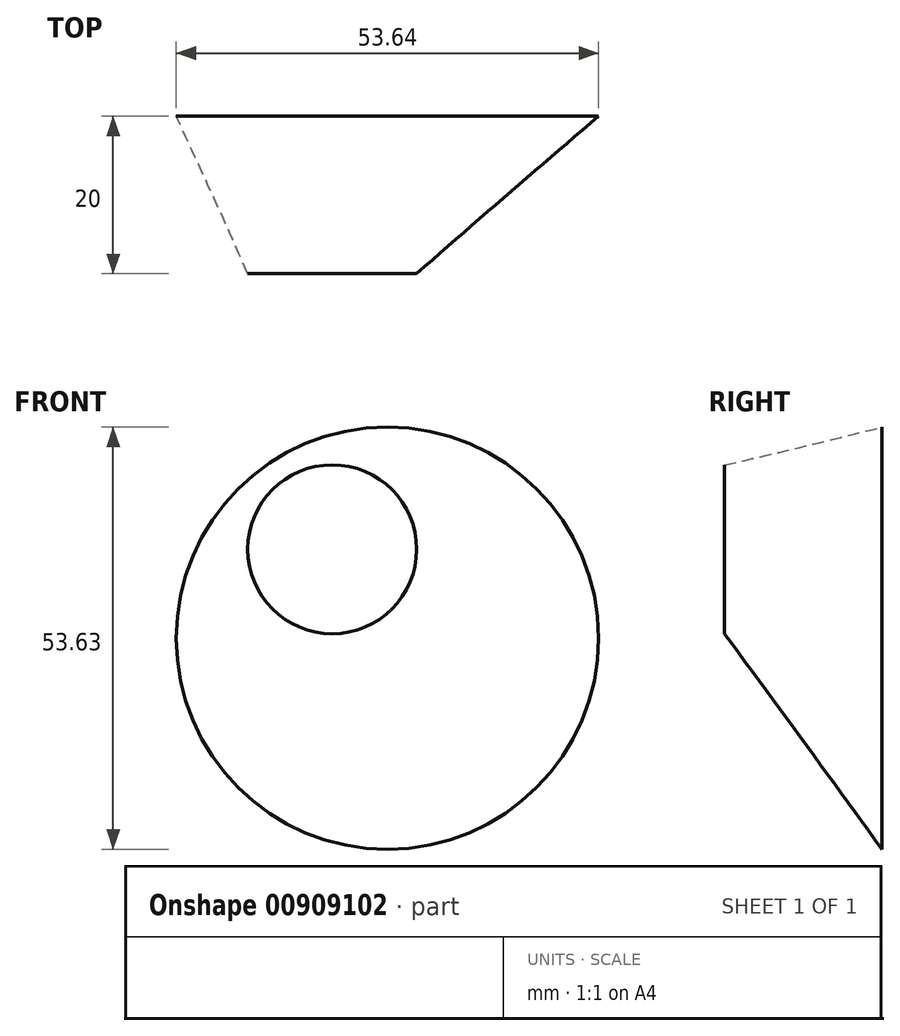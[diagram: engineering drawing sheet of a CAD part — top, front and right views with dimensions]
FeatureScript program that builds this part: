
annotation { "Feature Type Name" : "Feature", "Feature Type Description" : "" }
export const myFeature = defineFeature(function(context is Context, id is Id, definition is map)
    precondition{}
    {
        {
            var Q0;
            Q0=qCreatedBy(makeId("Front.planeOp"),FACE);
            var sketch = newSketch(context, id + "F0", { "sketchPlane" : qUnion([Q0])});
            skCircle(sketch, "E0", {"center": v(58.91, 25.92) * mm, "radius": 26.82 * mm});
            skSolve(sketch);
        }
        {
            var Q0;
            Q0=qCreatedBy(makeId("Front.planeOp"),FACE);
            cPlane(context, id + "F1", {"entities" : qUnion([Q0]), "cplaneType" : CPlaneType.OFFSET, "offset" : 20 * mm, "width" : 152.4 * mm, "height" : 152.4 * mm});
        }
        {
            var Q0;
            Q0=qCreatedBy(id+"F1.planeOp",FACE);
            var sketch = newSketch(context, id + "F2", { "sketchPlane" : qUnion([Q0])});
            skCircle(sketch, "E1", {"center": v(51.9, 37.2) * mm, "radius": 10.72 * mm});
            skSolve(sketch);
        }
        {
            var Q0;
            Q0=makeQuery(id+"F0.imprint","IMPRINT",FACE,{"disambiguationData":[TD([[makeQuery(id+"F0.imprint","IMPRINT",EDGE,{"derivedFrom":sQuery(id+"F0.wireOp",EDGE,"E0")}),1.0]])]});
            var Q1;
            Q1=makeQuery(id+"F2.imprint","IMPRINT",FACE,{"disambiguationData":[TD([[makeQuery(id+"F2.imprint","IMPRINT",EDGE,{"derivedFrom":sQuery(id+"F2.wireOp",EDGE,"E1")}),1.0]])]});
            loft(context, id + "F3", {"sheetProfilesArray" : [{ "sheetProfileEntities" : qUnion([Q0]) }, { "sheetProfileEntities" : qUnion([Q1]) }]});
        }
    });
